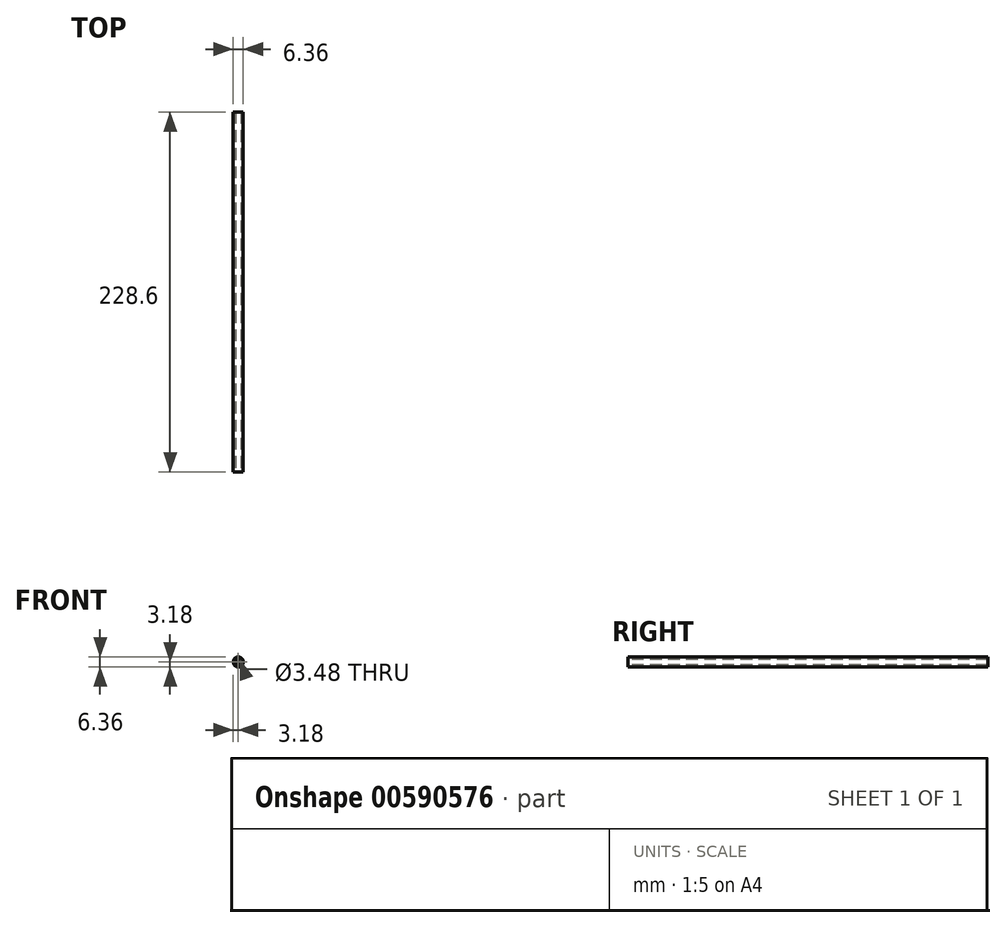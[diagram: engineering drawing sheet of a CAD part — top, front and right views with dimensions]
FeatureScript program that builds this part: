
annotation { "Feature Type Name" : "Feature", "Feature Type Description" : "" }
export const myFeature = defineFeature(function(context is Context, id is Id, definition is map)
    precondition{}
    {
        {
            var Q0;
            Q0=qCreatedBy(makeId("Front.planeOp"),FACE);
            var sketch = newSketch(context, id + "F0", { "sketchPlane" : qUnion([Q0])});
            skCircle(sketch, "E0", {"center": v(0, 0) * mm, "radius": 3.17 * mm});
            skCircle(sketch, "E1", {"center": v(0, 0) * mm, "radius": 1.74 * mm});
            skSolve(sketch);
        }
        {
            var Q0;
            Q0 = qSketchRegion(id + "F0", true);
            extrude(context, id + "F1", {"entities" : qUnion([Q0]), "oppositeDirection" : true, "depth" : 228.6 * mm, "offsetDistance" : 25.4 * mm});
        }
    });
